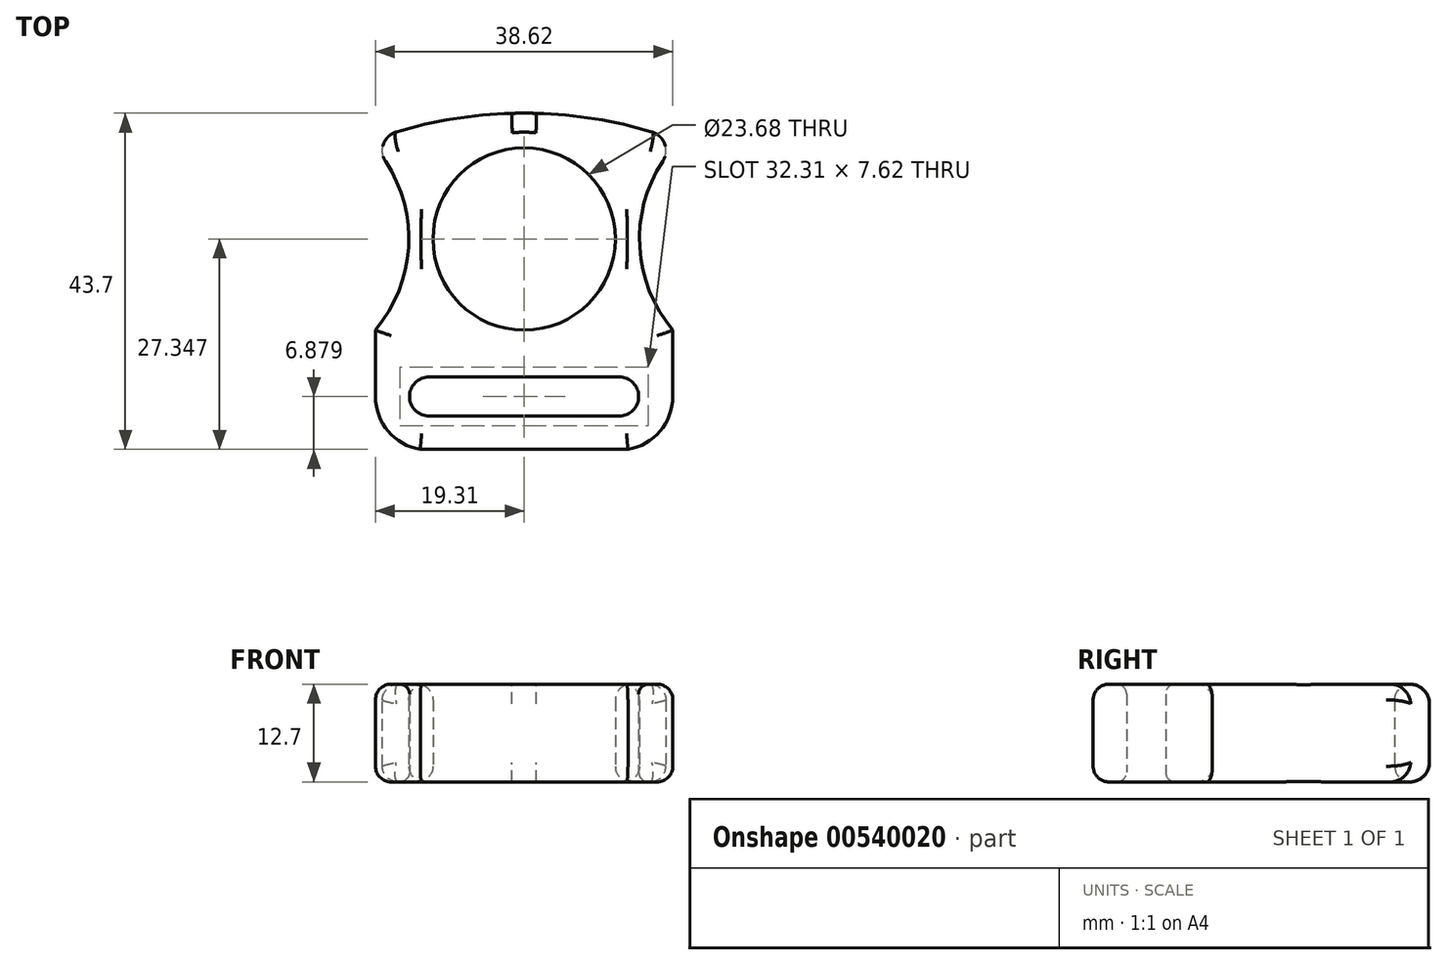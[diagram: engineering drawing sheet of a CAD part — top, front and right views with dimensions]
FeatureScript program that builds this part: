
annotation { "Feature Type Name" : "Feature", "Feature Type Description" : "" }
export const myFeature = defineFeature(function(context is Context, id is Id, definition is map)
    precondition{}
    {
        {
            var Q0;
            Q0=qCreatedBy(makeId("Top.planeOp"),FACE);
            var sketch = newSketch(context, id + "F0", { "sketchPlane" : qUnion([Q0])});
            skPoint(sketch, "E0.middle", {"position": v(0, 0) * mm});
            skCircle(sketch, "E1", {"center": v(0, 5.12) * mm, "radius": 11.84 * mm});
            skArc(sketch, "E2", {"start": v(19.31, 18.14) * mm, "mid": v(0, 21.47) * mm, "end": v(-19.31, 18.14) * mm});
            skPoint(sketch, "E3.startSnap0", {"position": v(0, 22.23) * mm});
            skArc(sketch, "E4", {"start": v(-19.31, -6.72) * mm, "mid": v(-14.98, 5.12) * mm, "end": v(-19.31, 16.96) * mm});
            skArc(sketch, "E5.MirrorCS", {"start": v(19.31, -6.72) * mm, "mid": v(14.98, 5.12) * mm, "end": v(19.31, 16.96) * mm});
            skLineSegment(sketch, "E6", {"start": v(-13.5, -22.23) * mm, "end": v(13.5, -22.23) * mm});
            skLineSegment(sketch, "E7", {"start": v(-19.31, 18.14) * mm, "end": v(-19.31, 16.96) * mm});
            skLineSegment(sketch, "E8", {"start": v(19.31, 18.14) * mm, "end": v(19.31, 16.96) * mm});
            skLineSegment(sketch, "E9", {"start": v(-19.31, -6.72) * mm, "end": v(-19.31, -15.35) * mm});
            skLineSegment(sketch, "E10", {"start": v(19.31, -6.72) * mm, "end": v(19.31, -15.35) * mm});
            skArc(sketch, "E11", {"start": v(-19.31, -15.35) * mm, "mid": v(-17.66, -19.86) * mm, "end": v(-13.5, -22.23) * mm});
            skArc(sketch, "E12.MirrorCS", {"start": v(19.31, -15.35) * mm, "mid": v(17.66, -19.86) * mm, "end": v(13.5, -22.23) * mm});
            skLineSegment(sketch, "E13", {"start": v(-12.35, -15.35) * mm, "end": v(12.35, -15.35) * mm});
            skArc(sketch, "E14.0.startCap", {"start": v(-12.35, -17.9) * mm, "mid": v(-14.89, -15.35) * mm, "end": v(-12.35, -12.81) * mm});
            skArc(sketch, "E14.0.endCap", {"start": v(12.35, -12.81) * mm, "mid": v(14.89, -15.35) * mm, "end": v(12.35, -17.9) * mm});
            skLineSegment(sketch, "E14.0.left", {"start": v(-12.35, -12.81) * mm, "end": v(12.35, -12.81) * mm});
            skLineSegment(sketch, "E14.0.right", {"start": v(-12.35, -17.9) * mm, "end": v(12.35, -17.9) * mm});
            skSolve(sketch);
        }
        {
            var Q0;
            Q0=makeQuery(id+"F0.imprint","IMPRINT",FACE,{"disambiguationData":[TD([[makeQuery(id+"F0.imprint","IMPRINT",EDGE,{"derivedFrom":sQuery(id+"F0.wireOp",EDGE,"E1")}),-1.0]])]});
            extrude(context, id + "F1", {"entities" : qUnion([Q0]), "depth" : 12.7 * mm, "offsetDistance" : 25.4 * mm});
        }
        {
            var Q0;
            Q0=makeQuery(id+"F1.opExtrude","CAP_EDGE",EDGE,{"disambiguationData":[OSD([sQuery(id+"F0.wireOp",EDGE,"E4")])],"isStart":false});
            var Q1;
            Q1=makeQuery(id+"F1.opExtrude","CAP_EDGE",EDGE,{"disambiguationData":[OSD([sQuery(id+"F0.wireOp",EDGE,"E9")])],"isStart":false});
            var Q2;
            Q2=makeQuery(id+"F1.opExtrude","CAP_EDGE",EDGE,{"disambiguationData":[OSD([sQuery(id+"F0.wireOp",EDGE,"E11")])],"isStart":false});
            var Q3;
            Q3=makeQuery(id+"F1.opExtrude","CAP_EDGE",EDGE,{"disambiguationData":[OSD([sQuery(id+"F0.wireOp",EDGE,"E6")])],"isStart":false});
            var Q4;
            Q4=makeQuery(id+"F1.opExtrude","CAP_EDGE",EDGE,{"disambiguationData":[OSD([sQuery(id+"F0.wireOp",EDGE,"E12.MirrorCS")])],"isStart":false});
            var Q5;
            Q5=makeQuery(id+"F1.opExtrude","CAP_EDGE",EDGE,{"disambiguationData":[OSD([sQuery(id+"F0.wireOp",EDGE,"E10")])],"isStart":false});
            var Q6;
            Q6=makeQuery(id+"F1.opExtrude","CAP_EDGE",EDGE,{"disambiguationData":[OSD([sQuery(id+"F0.wireOp",EDGE,"E5.MirrorCS")])],"isStart":false});
            var Q7;
            Q7=makeQuery(id+"F1.opExtrude","CAP_EDGE",EDGE,{"disambiguationData":[OSD([sQuery(id+"F0.wireOp",EDGE,"E1")])],"isStart":false});
            var Q8;
            Q8=makeQuery(id+"F1.opExtrude","CAP_EDGE",EDGE,{"disambiguationData":[OSD([sQuery(id+"F0.wireOp",EDGE,"E4")])],"isStart":true});
            var Q9;
            Q9=makeQuery(id+"F1.opExtrude","CAP_EDGE",EDGE,{"disambiguationData":[OSD([sQuery(id+"F0.wireOp",EDGE,"E9")])],"isStart":true});
            var Q10;
            Q10=makeQuery(id+"F1.opExtrude","CAP_EDGE",EDGE,{"disambiguationData":[OSD([sQuery(id+"F0.wireOp",EDGE,"E11")])],"isStart":true});
            var Q11;
            Q11=makeQuery(id+"F1.opExtrude","CAP_EDGE",EDGE,{"disambiguationData":[OSD([sQuery(id+"F0.wireOp",EDGE,"E5.MirrorCS")])],"isStart":true});
            var Q12;
            Q12=makeQuery(id+"F1.opExtrude","CAP_EDGE",EDGE,{"disambiguationData":[OSD([sQuery(id+"F0.wireOp",EDGE,"E10")])],"isStart":true});
            var Q13;
            Q13=makeQuery(id+"F1.opExtrude","CAP_EDGE",EDGE,{"disambiguationData":[OSD([sQuery(id+"F0.wireOp",EDGE,"E12.MirrorCS")])],"isStart":true});
            var Q14;
            Q14=makeQuery(id+"F1.opExtrude","CAP_EDGE",EDGE,{"disambiguationData":[OSD([sQuery(id+"F0.wireOp",EDGE,"E6")])],"isStart":true});
            var Q15;
            Q15=makeQuery(id+"F1.opExtrude","CAP_EDGE",EDGE,{"disambiguationData":[OSD([sQuery(id+"F0.wireOp",EDGE,"E1")])],"isStart":true});
            fillet(context, id + "F2", {"entities" : qUnion([Q0, Q1, Q2, Q3, Q4, Q5, Q6, Q7, Q8, Q9, Q10, Q11, Q12, Q13, Q14, Q15]), "radius" : 2.03 * mm, "tangentPropagation" : true, "allowEdgeOverflow" : false});
        }
        {
            var Q0;
            Q0=makeQuery(id+"F1.opExtrude","SWEPT_FACE",FACE,{"disambiguationData":[OSD([sQuery(id+"F0.wireOp",EDGE,"E2")])]});
            fillet(context, id + "F3", {"entities" : qUnion([Q0]), "radius" : 2.54 * mm, "tangentPropagation" : true, "allowEdgeOverflow" : false});
        }
        {
            var Q0;
            Q0=makeQuery(id+"F1.opExtrude","CAP_EDGE",EDGE,{"disambiguationData":[OSD([sQuery(id+"F0.wireOp",EDGE,"E14.0.left")])],"isStart":false});
            var Q1;
            Q1=makeQuery(id+"F1.opExtrude","CAP_EDGE",EDGE,{"disambiguationData":[OSD([sQuery(id+"F0.wireOp",EDGE,"E14.0.startCap")])],"isStart":false});
            var Q2;
            Q2=makeQuery(id+"F1.opExtrude","CAP_EDGE",EDGE,{"disambiguationData":[OSD([sQuery(id+"F0.wireOp",EDGE,"E14.0.right")])],"isStart":false});
            var Q3;
            Q3=makeQuery(id+"F1.opExtrude","CAP_EDGE",EDGE,{"disambiguationData":[OSD([sQuery(id+"F0.wireOp",EDGE,"E14.0.endCap")])],"isStart":false});
            var Q4;
            Q4=makeQuery(id+"F1.opExtrude","CAP_EDGE",EDGE,{"disambiguationData":[OSD([sQuery(id+"F0.wireOp",EDGE,"E14.0.left")])],"isStart":true});
            var Q5;
            Q5=makeQuery(id+"F1.opExtrude","CAP_EDGE",EDGE,{"disambiguationData":[OSD([sQuery(id+"F0.wireOp",EDGE,"E14.0.endCap")])],"isStart":true});
            var Q6;
            Q6=makeQuery(id+"F1.opExtrude","CAP_EDGE",EDGE,{"disambiguationData":[OSD([sQuery(id+"F0.wireOp",EDGE,"E14.0.right")])],"isStart":true});
            var Q7;
            Q7=makeQuery(id+"F1.opExtrude","CAP_EDGE",EDGE,{"disambiguationData":[OSD([sQuery(id+"F0.wireOp",EDGE,"E14.0.startCap")])],"isStart":true});
            fillet(context, id + "F4", {"entities" : qUnion([Q0, Q1, Q2, Q3, Q4, Q5, Q6, Q7]), "radius" : 1.27 * mm, "tangentPropagation" : true, "allowEdgeOverflow" : false});
        }
    });
